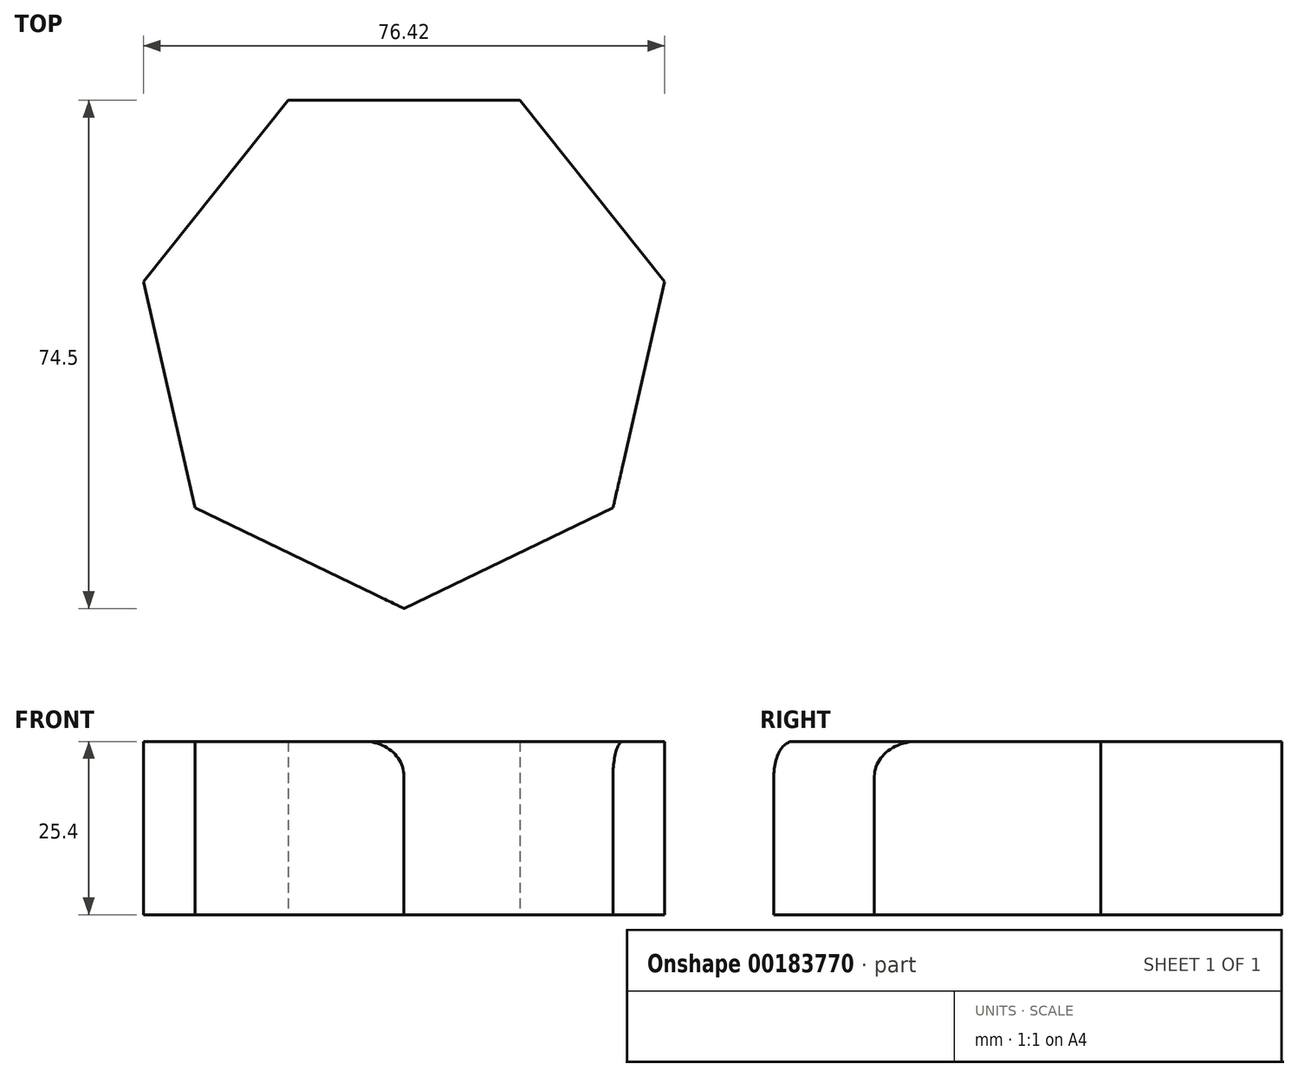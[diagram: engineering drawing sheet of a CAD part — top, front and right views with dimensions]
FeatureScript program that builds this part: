
annotation { "Feature Type Name" : "Feature", "Feature Type Description" : "" }
export const myFeature = defineFeature(function(context is Context, id is Id, definition is map)
    precondition{}
    {
        {
            var Q0;
            Q0=qCreatedBy(makeId("Top.planeOp"),FACE);
            var sketch = newSketch(context, id + "F0", { "sketchPlane" : qUnion([Q0])});
            skCircle(sketch, "E0.cCircle", {"center": v(0, 0) * mm, "radius": 35.31 * mm, "construction": true});
            skLineSegment(sketch, "E0.0", {"start": v(-17, 35.31) * mm, "end": v(17, 35.31) * mm});
            skLineSegment(sketch, "E0.1", {"start": v(17, 35.31) * mm, "end": v(38.2, 8.72) * mm});
            skLineSegment(sketch, "E0.2", {"start": v(38.2, 8.72) * mm, "end": v(30.64, -24.44) * mm});
            skLineSegment(sketch, "E0.3", {"start": v(30.64, -24.44) * mm, "end": v(0, -39.2) * mm});
            skLineSegment(sketch, "E0.4", {"start": v(0, -39.2) * mm, "end": v(-30.64, -24.44) * mm});
            skLineSegment(sketch, "E0.5", {"start": v(-30.64, -24.44) * mm, "end": v(-38.2, 8.72) * mm});
            skLineSegment(sketch, "E0.6", {"start": v(-38.2, 8.72) * mm, "end": v(-17, 35.31) * mm});
            skPoint(sketch, "E0.0.midPoint", {"position": v(0, 35.31) * mm});
            skSolve(sketch);
        }
        {
            var Q0;
            Q0=makeQuery(id+"F0.imprint","IMPRINT",FACE,{"disambiguationData":[TD([[makeQuery(id+"F0.imprint","IMPRINT",EDGE,{"derivedFrom":sQuery(id+"F0.wireOp",EDGE,"E0.0")}),-1.0]])]});
            extrude(context, id + "F1", {"entities" : qUnion([Q0]), "depth" : 25.4 * mm});
        }
        {
            var Q0;
            Q0=makeQuery(id+"F1.opExtrude","CAP_EDGE",EDGE,{"disambiguationData":[OSD([sQuery(id+"F0.wireOp",EDGE,"E0.3")])],"isStart":false});
            fillet(context, id + "F2", {"entities" : qUnion([Q0]), "radius" : 5.08 * mm, "tangentPropagation" : true, "allowEdgeOverflow" : false});
        }
    });
